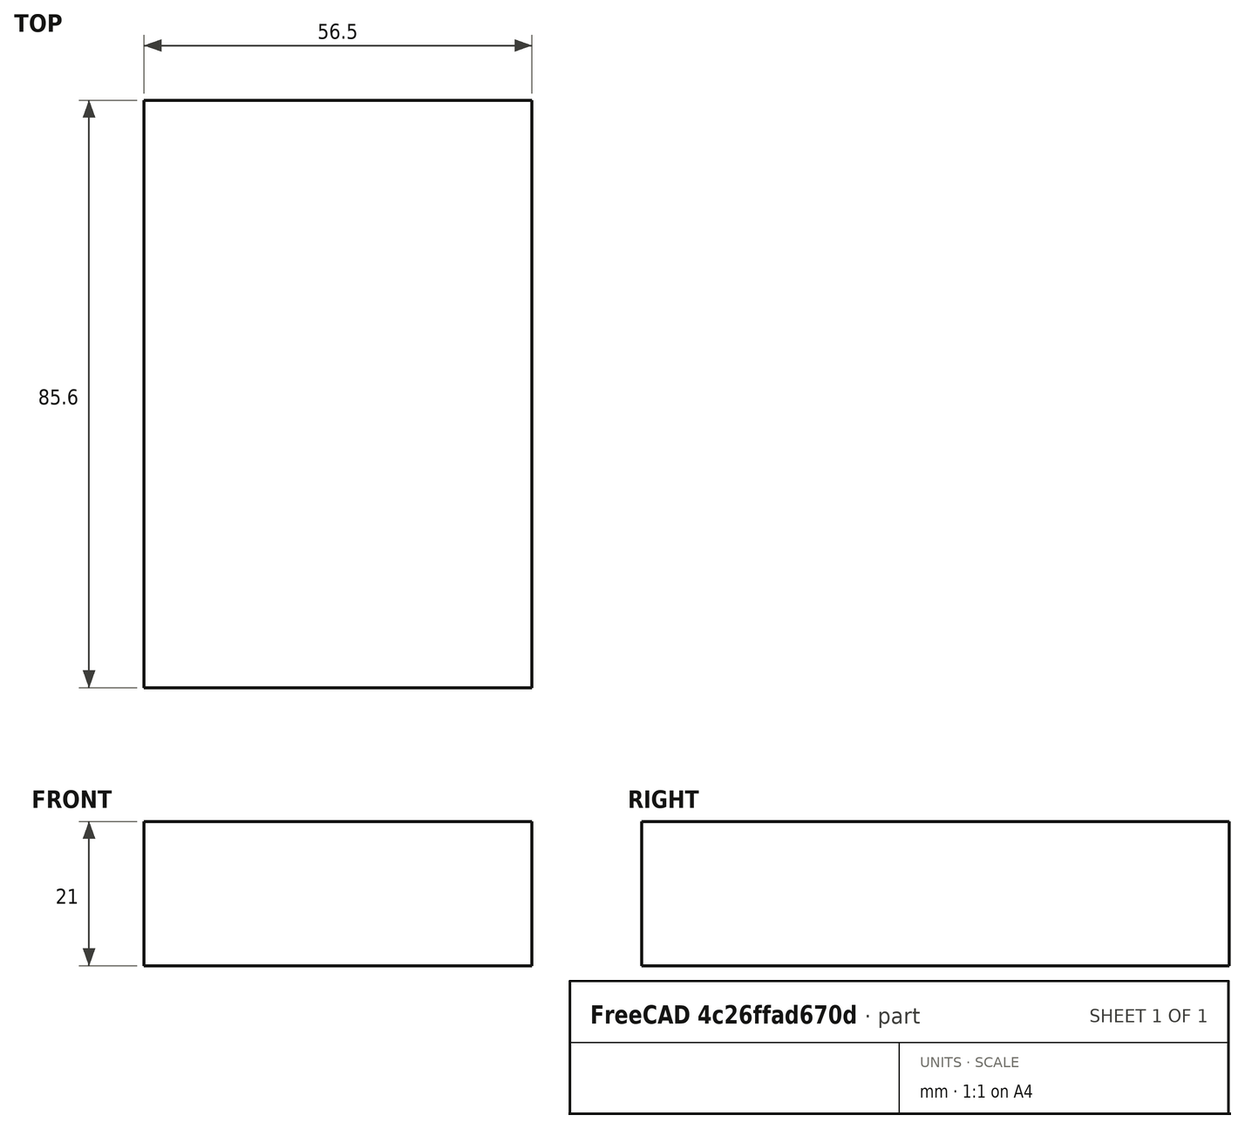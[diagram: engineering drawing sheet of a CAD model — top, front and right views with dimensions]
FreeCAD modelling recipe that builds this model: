
FCSTD DOCUMENT  (FreeCAD 1.0R39319 (Git))
Label: pi-rough
License: All rights reserved
LicenseURL: http://en.wikipedia.org/wiki/All_rights_reserved
objects: Spreadsheet::Sheet×1, Sketcher::SketchObject×1, PartDesign::Pad×1, PartDesign::Body×1
note: 6 computed .brp shape members not serialized (recipe doc carries the construction recipe); baked Part::Feature solids carry a one-line shape summary decoded from their .brp

FEATURE [Spreadsheet::Sheet] Spreadsheet
  cells = A2='Length; B2(Length)=85.6; A3='Width; B3(Width)=56.5; A4='Height; B4(Height)=21
FEATURE [Sketcher::SketchObject] Sketch
  ArcFitTolerance = 1e-06
  AttachmentSupport = -> [XY_Plane]
  FullyConstrained = true
  MakeInternals = false
  MapMode = 5
  expr: Constraints[8] = Spreadsheet.Width
  expr: Constraints[9] = Spreadsheet.Length
  sketch-geometry (4):
    g0: LineSegment StartX=8 StartY=55.6 StartZ=0 EndX=8 EndY=-30 EndZ=0
    g1: LineSegment StartX=8 StartY=-30 StartZ=0 EndX=64.5 EndY=-30 EndZ=0
    g2: LineSegment StartX=64.5 StartY=-30 StartZ=0 EndX=64.5 EndY=55.6 EndZ=0
    g3: LineSegment StartX=64.5 StartY=55.6 StartZ=0 EndX=8 EndY=55.6 EndZ=0
  constraints (12):
    c: Coincident(g0,g1)
    c: Coincident(g1,g2)
    c: Coincident(g2,g3)
    c: Coincident(g3,g0)
    c: Vertical(g0)
    c: Vertical(g2)
    c: Horizontal(g1)
    c: Horizontal(g3)
    c: DistanceX(g0,g1) = 56.5
    c: DistanceY(g0,g0) = 85.6
    c: DistanceY(g0,g-1) = 30
    c: DistanceX(g-1,g0) = 8
FEATURE [PartDesign::Pad] Pad
  Direction = (0,0,1)
  Length = 21
  Length2 = 10
  Profile = -> Sketch
  ReferenceAxis = -> Sketch [N_Axis]
  Suppressed = false
  Type = 0
  expr: Length = Spreadsheet.Height
FEATURE [PartDesign::Body] Body
  AllowCompound = false
  Group = -> [Sketch,Pad]
  Origin = -> Origin
  Tip = -> Pad
